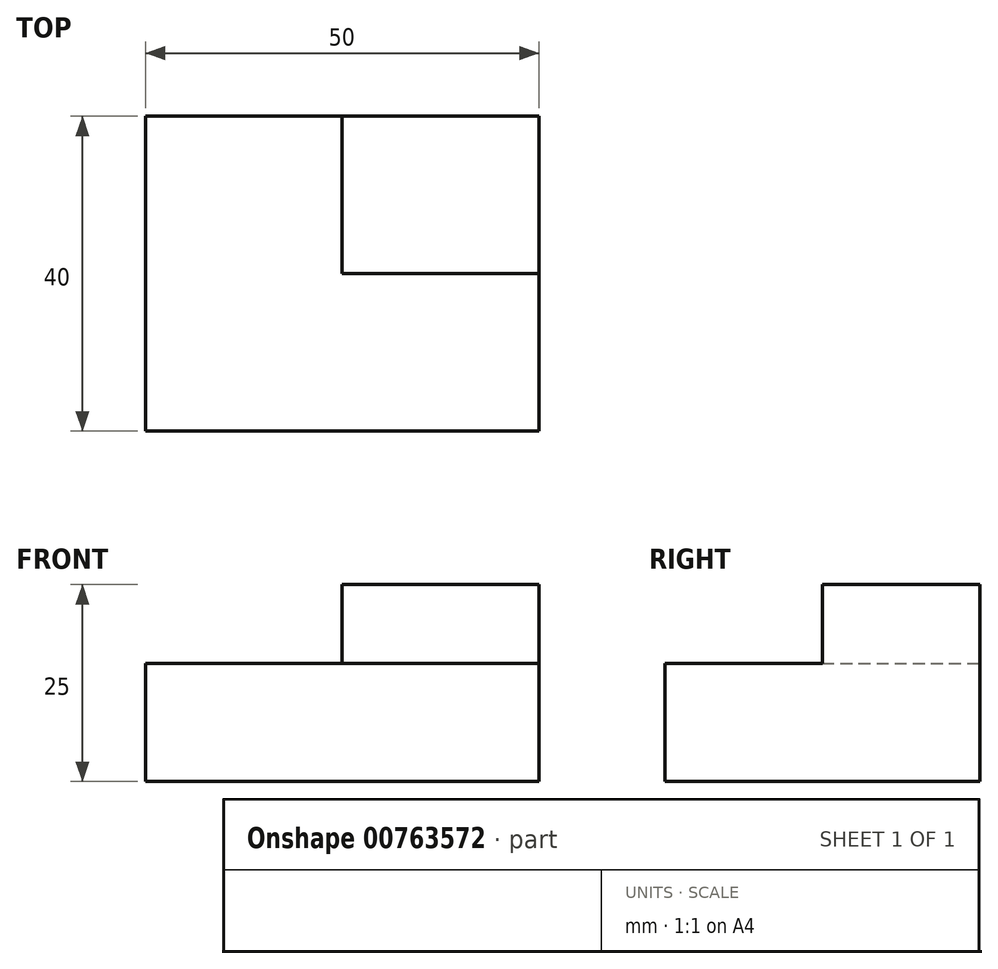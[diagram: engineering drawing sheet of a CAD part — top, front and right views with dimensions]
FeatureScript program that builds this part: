
annotation { "Feature Type Name" : "Feature", "Feature Type Description" : "" }
export const myFeature = defineFeature(function(context is Context, id is Id, definition is map)
    precondition{}
    {
        {
            var Q0;
            Q0=qCreatedBy(makeId("Top.planeOp"),FACE);
            var sketch = newSketch(context, id + "F0", { "sketchPlane" : qUnion([Q0])});
            skLineSegment(sketch, "E0.bottom", {"start": v(25, -20) * mm, "end": v(-25, -20) * mm});
            skLineSegment(sketch, "E0.top", {"start": v(25, 20) * mm, "end": v(-25, 20) * mm});
            skLineSegment(sketch, "E0.left", {"start": v(25, -20) * mm, "end": v(25, 20) * mm});
            skLineSegment(sketch, "E0.right", {"start": v(-25, -20) * mm, "end": v(-25, 20) * mm});
            skPoint(sketch, "E0.middle", {"position": v(0, 0) * mm});
            skSolve(sketch);
        }
        {
            var Q0;
            Q0=makeQuery(id+"F0.imprint","IMPRINT",FACE,{"disambiguationData":[TD([[makeQuery(id+"F0.imprint","IMPRINT",EDGE,{"derivedFrom":sQuery(id+"F0.wireOp",EDGE,"E0.bottom")}),-1.0]])]});
            extrude(context, id + "F1", {"entities" : qUnion([Q0]), "depth" : 25 * mm, "offsetDistance" : 25 * mm});
        }
        {
            var Q0;
            Q0=makeQuery(id+"F1.opExtrude","CAP_FACE",FACE,{"disambiguationData":[OSD([sQuery(id+"F0.wireOp",EDGE,"E0.bottom"),sQuery(id+"F0.wireOp",EDGE,"E0.top"),sQuery(id+"F0.wireOp",EDGE,"E0.left"),sQuery(id+"F0.wireOp",EDGE,"E0.right")])],"isStart":false});
            var sketch = newSketch(context, id + "F2", { "sketchPlane" : qUnion([Q0])});
            skLineSegment(sketch, "E1.bottom", {"start": v(0, 0) * mm, "end": v(25, 0) * mm});
            skLineSegment(sketch, "E1.top", {"start": v(0, 20) * mm, "end": v(25, 20) * mm});
            skLineSegment(sketch, "E1.left", {"start": v(0, 0) * mm, "end": v(0, 20) * mm});
            skLineSegment(sketch, "E1.right", {"start": v(25, 0) * mm, "end": v(25, 20) * mm});
            skSolve(sketch);
        }
        {
            var Q0;
            {var subQ4=sQuery(id+"F2.wireOp",EDGE,"E1.bottom");Q0=makeQuery(id+"F2.imprint","IMPRINT",FACE,{"disambiguationData":[TD([[makeQuery(id+"F2.imprint","IMPRINT",EDGE,{"derivedFrom":subQ4}),-1.0]])]});}
            extrude(context, id + "F3", {"entities" : qUnion([Q0]), "operationType" : NewBodyOperationType.REMOVE, "oppositeDirection" : true, "depth" : 10 * mm, "offsetDistance" : 25 * mm});
        }
    });
